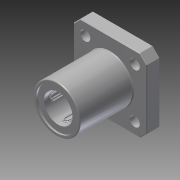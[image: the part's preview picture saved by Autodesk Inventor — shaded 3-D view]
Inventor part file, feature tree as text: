
AUTODESK INVENTOR PART (.ipt)
format: ipt  version: 2014 (Build 180170000, 170)  size: 1,717,248 bytes
history: native  units: in
note: dims shown in document units (in); Inventor stores cm internally (conversion verified against a paired STEP export)
features: chamfer x1, other x1, imported_body x1
ambient origin geometry x8: Origin, YZ Plane, XZ Plane, XY Plane, X Axis, Y Axis, Z Axis, Center Point
bodies: Body1 (feature_tree)
feature tree (3):
  chamfer  "Chamfer1"  [1 undecoded]
  other  "6483K6301"
  imported_body  "Base1"
note: 1 required parameter value undecoded (feature->parameter linkage not recoverable at this tier; creation-order binding heuristic only, values carry confidence <= 0.55)
